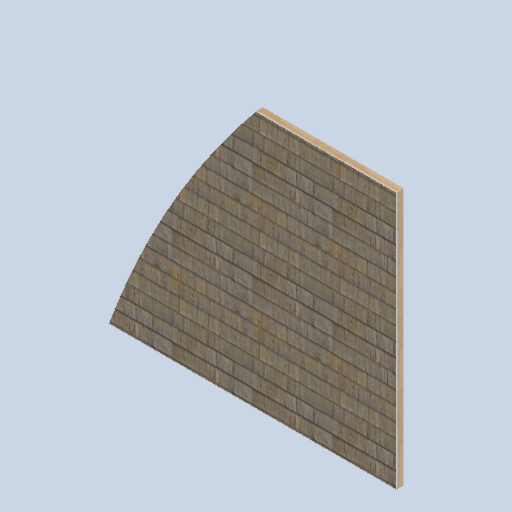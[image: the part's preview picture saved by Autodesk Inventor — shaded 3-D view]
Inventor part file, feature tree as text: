
AUTODESK INVENTOR PART (.ipt)
format: ipt  version: 2024.2 (Build 282272000, 272)  size: 237,056 bytes
history: native  units: in
note: dims shown in document units (in); Inventor stores cm internally (conversion verified against a paired STEP export)
features: other x3, sketch x1
ambient origin geometry x8: Origin, YZ Plane, XZ Plane, XY Plane, X Axis, Y Axis, Z Axis, Center Point
bodies: Solid1 (feature_tree)
feature tree (4):
  other  "front_wall_block02_MIR.ipt"
  other  "Solid1::front_wall_block02_MIR.ipt"
  other  "TaggingFeature1"
  sketch  "Sketch1"  dims[d0=0.3937in]
